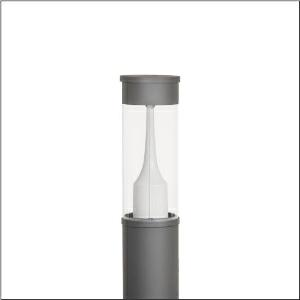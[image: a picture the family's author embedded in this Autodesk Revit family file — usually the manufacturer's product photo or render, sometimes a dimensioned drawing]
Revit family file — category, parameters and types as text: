
# Revit family: city-light_120_iq___p1_0a_5xa5285ff14h_303b
name_source: partatom
category: Lighting Fixtures
units: mm (PartAtom-declared; Revit-internal decimal feet)

## family parameters
Cut with Voids When Loaded = No
Host = Face
Light Source = No
Part Type = Normal
Room Calculation Point = No
Round Connector Dimension = Use Diameter
Shared = No

## types (1)
- --- (1 x LED, 1510 lm, 10.5 W, 3000K)
    Apparent Load = 11 VA
    CIE Flux Codes = 32 61 90 93 100
    Color Rendering = 70
    Color Temperature = 3000K
    Default Elevation = 1800 mm
    Description = City-Light 120 iQ, bollard luminaire, Module 540 iQ-SR, primary light control with 3 zone facetted reflector, of plastic, silver coated, highly specular, structured, primary optical cover: cover, of PMMA, transparent, light distribution: P1.0a, primary light characteristic: strongly asymmetric, LED, High Power LED, rated luminous flux: 1.510lm, luminous efficacy: 144lm/W, light colour: 730, colour temperature: 3000K, control gear: ECG iQ, control: Auto-Match, Temp-Guard, Lumen-Switch, Night-Set, Smart-Wire, Light-Fading, Desk-Remote (wireless, voltage-free reading and setting of iQ features in the workshop via application-optimized NFC function/RFID function), optimised constant luminous flux control (CLO 2.0), Street-Remote, pre-setting: logarithmic dimming characteristic, with terminal, 6-pole, max. 2.5mm², mains connection: 230..240V, AC, 50/60Hz, start of lifetime: 11W, end of service life: 11W, reduction: 5W, luminaire housing, cylindrical, of extruded aluminium section, coated, Siteco® metallic grey (DB 702S), length: 1.200mm, diameter: 200mm, Module 540 iQ-SR, traffic white (RAL 9016), equipment: standard, protection rating (complete): IP54, insulation class (complete): insulation class II (safety insulation), certification: CE, ENEC, VDE, packaging unit: 1 piece

Light Distribution: P1.0a
    Height = 500 mm
    Lamp = 1 x LED
    Lamp Light Flux = 1510 lm
    Lamp Power = 10.5 W
    Lamp count = 1
    Length = 200 mm  [stored 0.656168 ft]
    Luminous efficacy = 144 lm/W
    Manufacturer = Siteco
    ModVariant = No
    Model = 5XA5285FF14H
    Mounting Place = Floor
    Mounting Type = Freestanding
    Number of Poles = 1
    OnlyDefault = Yes
    Power Factor = 1
    Product Name = City-Light 120 iQ | P1.0a
    Product group = bollard luminaire
    ProductGroupID = 1304
    Protection Class = Protection class II
    Protection Degree = IP 54
    RLX_Detail_Level = 1
    RLX_Emergency_Light_Flux = 0 lm
    RLX_Emergency_Type = 0
    RLX_Emergency_Type_DB = No
    RlxData = <blob elided: 52493 chars, md5=9d11d7f6>
    Socket = socket
    Standby Power = 0 W
    System Light Flux = 1510 lm
    System Power = 11 W
    Type Comments = factory setting: luminous flux: 100 % | dim-lin: 254 | 419 mA
    Type Image = l_1006922.jpg
    URL = http://relux.com
    VarID = @adj_129953
    Voltage = 0 V
    Weight = 0.00 kg
    Width = 0 mm  [stored 0 ft]

note: [stored X ft] marks values corroborated as IEEE doubles in the binary element streams (Revit-internal decimal feet)

## geometry (parser evidence)
native form markers: Blend x4, Sweep x10
no freeform markers — native parametric forms only
